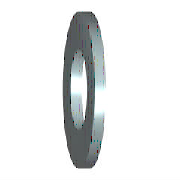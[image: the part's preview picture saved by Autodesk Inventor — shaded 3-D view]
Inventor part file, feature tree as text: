
AUTODESK INVENTOR PART (.ipt)
format: ipt  version: 2025 (Build 290162010, 162A)  size: 108,544 bytes
history: native  units: mm (DEFAULTED — no unit token found)
features: other x1, plane x1
ambient origin geometry x7: Origin, YZ Plane, XY Plane, X Axis, Y Axis, Z Axis, Center Point
bodies: Solid1 (feature_tree), Body (feature_tree)
feature tree (2):
  other  "Work Axis1"
  plane  "Work Plane1"
